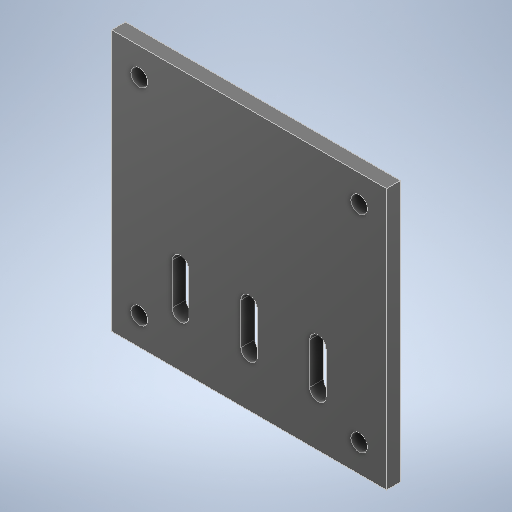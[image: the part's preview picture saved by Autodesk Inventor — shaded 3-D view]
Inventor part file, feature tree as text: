
AUTODESK INVENTOR PART (.ipt)
format: ipt  version: 2025.1 (Build 291241020, 241B)  size: 402,432 bytes
history: native  units: mm
features: sketch x2, extrude x2, hole x1
ambient origin geometry x8: Origin, YZ Plane, XZ Plane, XY Plane, X Axis, Y Axis, Z Axis, Center Point
bodies: Solid1 (feature_tree)
feature tree (5):
  sketch  "Sketch1"  dims[d0=100.0mm d1=95.0mm]
  extrude  "Extrusion1"  Depth=95.0mm
  hole  "Hole1"  [1 undecoded]
  extrude  "Extrusion2"  Depth=10.0mm
  sketch  "Sketch2"  dims[d2=5.0mm d3=0.0mm d4=75.0mm d5=10.0mm d6=80.0mm d7=10.0mm d8=6.0mm d9=6.0mm d10=4.0mm d11=2.0mm d12=90.0deg d13=8.0mm d14=20.594885mm d15=50.0mm d17=25.0mm d18=25.0mm d19=69.099mm d27=6.0mm d28=15.0mm d29=7.5mm d30=10.0mm d31=0.0mm]
note: 1 required parameter value undecoded (feature->parameter linkage not recoverable at this tier; creation-order binding heuristic only, values carry confidence <= 0.55)
